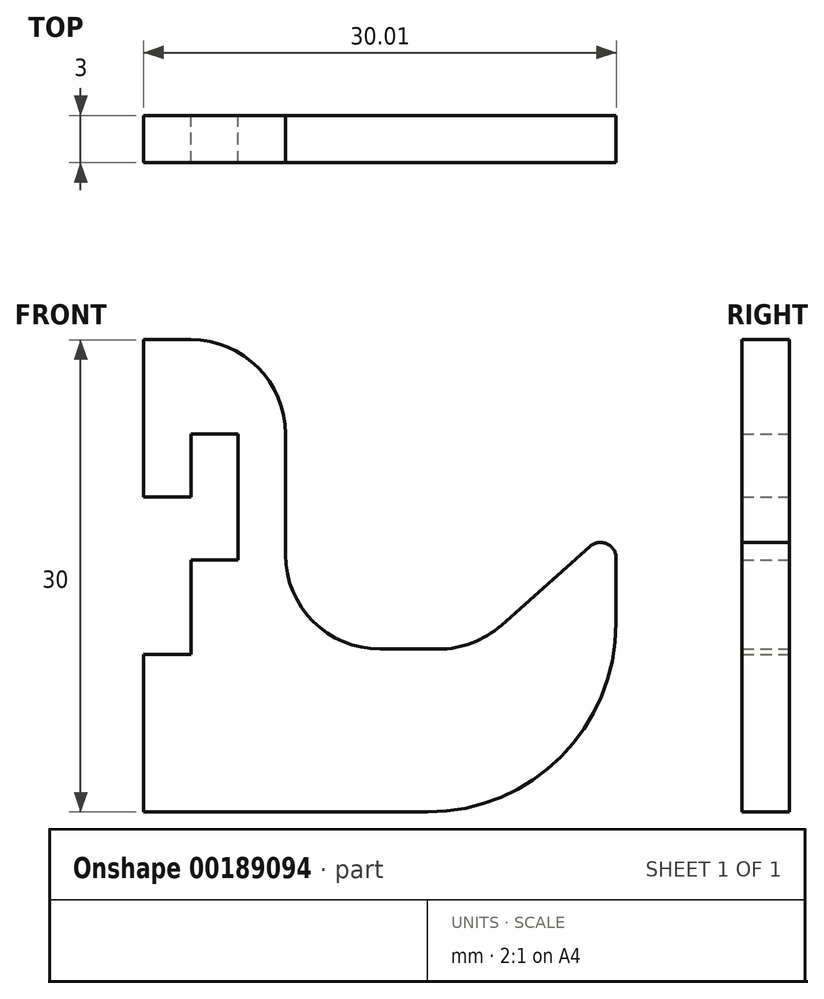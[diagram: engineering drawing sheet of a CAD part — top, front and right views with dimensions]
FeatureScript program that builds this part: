
annotation { "Feature Type Name" : "Feature", "Feature Type Description" : "" }
export const myFeature = defineFeature(function(context is Context, id is Id, definition is map)
    precondition{}
    {
        {
            var Q0;
            Q0=qCreatedBy(makeId("Front.planeOp"),FACE);
            var sketch = newSketch(context, id + "F0", { "sketchPlane" : qUnion([Q0])});
            skLineSegment(sketch, "E0", {"start": v(-9.32, -14.44) * mm, "end": v(8.69, -14.44) * mm});
            skLineSegment(sketch, "E1", {"start": v(20.69, -2.44) * mm, "end": v(20.69, 1.68) * mm});
            skLineSegment(sketch, "E2", {"start": v(19.02, 2.43) * mm, "end": v(13.39, -2.57) * mm});
            skLineSegment(sketch, "E3", {"start": v(9.4, -4.09) * mm, "end": v(5.68, -4.09) * mm});
            skLineSegment(sketch, "E4", {"start": v(-0.32, 1.91) * mm, "end": v(-0.32, 9.56) * mm});
            skLineSegment(sketch, "E5", {"start": v(-6.32, 15.56) * mm, "end": v(-9.32, 15.56) * mm});
            skLineSegment(sketch, "E6", {"start": v(-9.32, 15.56) * mm, "end": v(-9.32, 5.56) * mm});
            skLineSegment(sketch, "E7", {"start": v(-9.32, 5.56) * mm, "end": v(-6.32, 5.56) * mm});
            skLineSegment(sketch, "E8", {"start": v(-6.32, 1.56) * mm, "end": v(-6.32, -4.44) * mm});
            skLineSegment(sketch, "E9", {"start": v(-6.32, -4.44) * mm, "end": v(-9.32, -4.44) * mm});
            skLineSegment(sketch, "E10", {"start": v(-9.32, -4.44) * mm, "end": v(-9.32, -14.44) * mm});
            skPoint(sketch, "E11.visualSharp", {"position": v(-0.32, 15.56) * mm});
            skArc(sketch, "E11.filletArc", {"start": v(-0.32, 9.56) * mm, "mid": v(-2.07, 13.8) * mm, "end": v(-6.32, 15.56) * mm});
            skPoint(sketch, "E12.visualSharp", {"position": v(20.69, 3.91) * mm});
            skArc(sketch, "E12.filletArc", {"start": v(20.69, 1.68) * mm, "mid": v(20.1, 2.6) * mm, "end": v(19.02, 2.43) * mm});
            skPoint(sketch, "E13.visualSharp", {"position": v(11.68, -4.09) * mm});
            skArc(sketch, "E13.filletArc", {"start": v(9.4, -4.09) * mm, "mid": v(11.53, -3.7) * mm, "end": v(13.39, -2.57) * mm});
            skPoint(sketch, "E14.visualSharp", {"position": v(-0.32, -4.09) * mm});
            skArc(sketch, "E14.filletArc", {"start": v(-0.32, 1.91) * mm, "mid": v(1.44, -2.33) * mm, "end": v(5.68, -4.09) * mm});
            skPoint(sketch, "E15.visualSharp", {"position": v(20.69, -14.44) * mm});
            skArc(sketch, "E15.filletArc", {"start": v(8.69, -14.44) * mm, "mid": v(17.17, -10.92) * mm, "end": v(20.69, -2.44) * mm});
            skLineSegment(sketch, "E16", {"start": v(-6.32, 5.56) * mm, "end": v(-6.32, 9.56) * mm});
            skLineSegment(sketch, "E17", {"start": v(-6.32, 9.56) * mm, "end": v(-3.32, 9.56) * mm});
            skLineSegment(sketch, "E18", {"start": v(-3.32, 9.56) * mm, "end": v(-3.32, 1.56) * mm});
            skLineSegment(sketch, "E19", {"start": v(-3.32, 1.56) * mm, "end": v(-6.32, 1.56) * mm});
            skSolve(sketch);
        }
        {
            var Q0;
            Q0=makeQuery(id+"F0.imprint","IMPRINT",FACE,{"disambiguationData":[TD([[makeQuery(id+"F0.imprint","IMPRINT",EDGE,{"derivedFrom":sQuery(id+"F0.wireOp",EDGE,"E0")}),1.0]])]});
            extrude(context, id + "F1", {"entities" : qUnion([Q0]), "depth" : 3 * mm});
        }
    });
